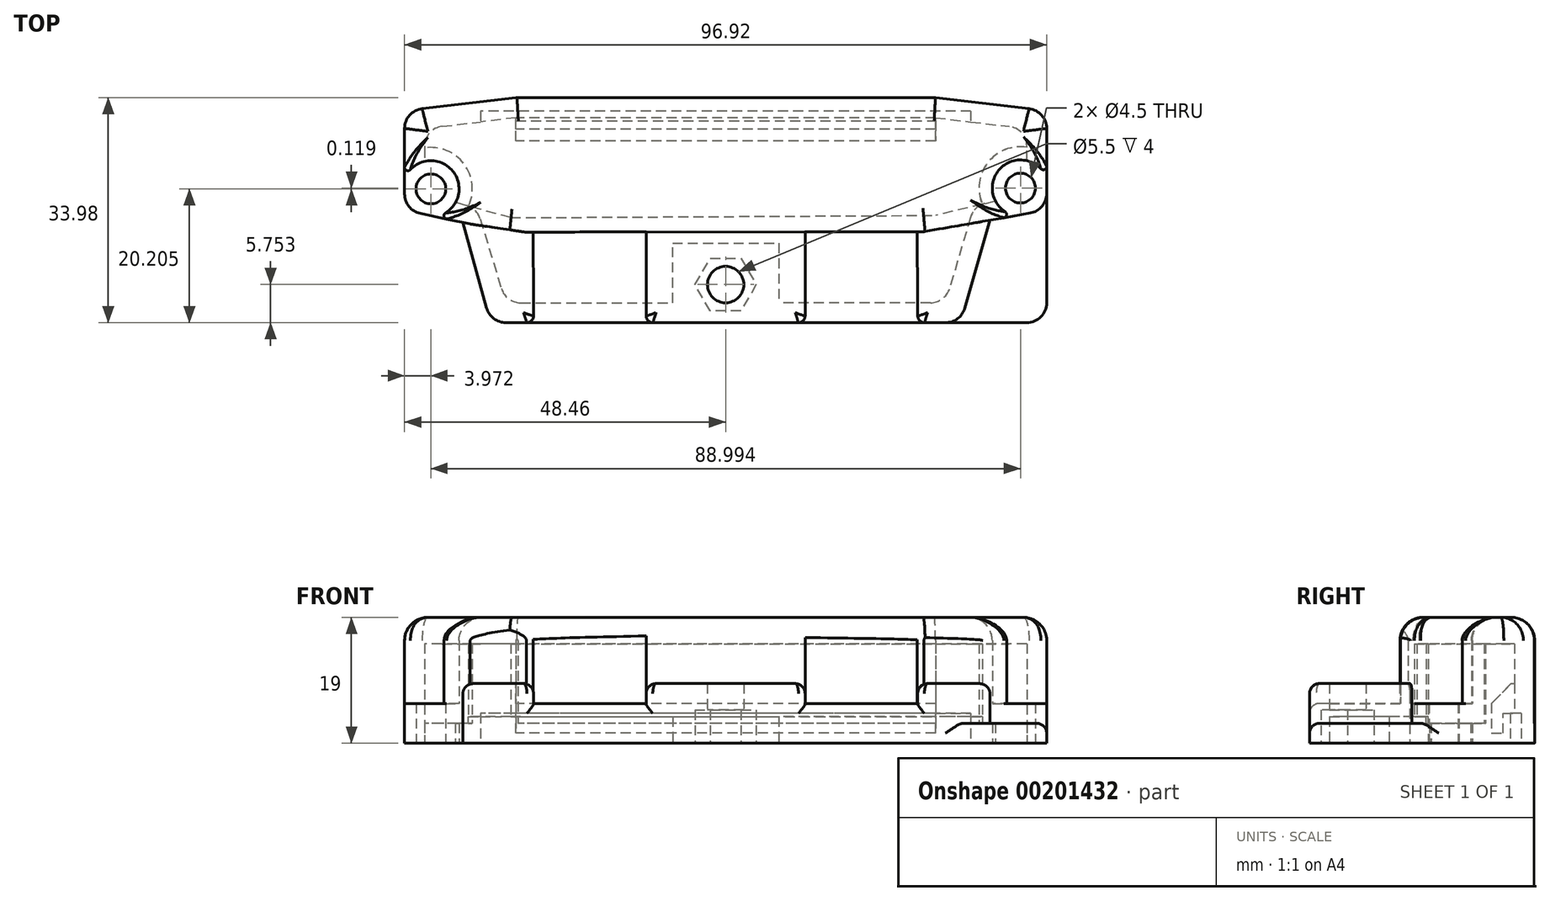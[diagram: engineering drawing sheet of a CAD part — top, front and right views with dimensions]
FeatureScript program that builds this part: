
annotation { "Feature Type Name" : "Feature", "Feature Type Description" : "" }
export const myFeature = defineFeature(function(context is Context, id is Id, definition is map)
    precondition{}
    {
        {
            var Q0;
            Q0=qCreatedBy(makeId("Top.planeOp"),FACE);
            var sketch = newSketch(context, id + "F0", { "sketchPlane" : qUnion([Q0])});
            skLineSegment(sketch, "E0.bottom", {"start": v(31.33, 16.99) * mm, "end": v(-31.32, 16.99) * mm});
            skLineSegment(sketch, "E0.left", {"start": v(48.46, 12.34) * mm, "end": v(48.46, 2.53) * mm});
            skLineSegment(sketch, "E0.right", {"start": v(-48.46, 12.34) * mm, "end": v(-48.46, 2.43) * mm});
            skPoint(sketch, "E0.middle", {"position": v(0, 0) * mm});
            skLineSegment(sketch, "E1", {"start": v(-45.8, 15.32) * mm, "end": v(-31.67, 16.97) * mm});
            skLineSegment(sketch, "E2", {"start": v(45.81, 15.32) * mm, "end": v(31.68, 16.97) * mm});
            skPoint(sketch, "E3.orphan", {"position": v(-48.46, 16.99) * mm});
            skPoint(sketch, "E4.orphan", {"position": v(48.46, 16.99) * mm});
            skPoint(sketch, "E5.visualSharp", {"position": v(-48.46, 15.01) * mm});
            skArc(sketch, "E5.filletArc", {"start": v(-45.8, 15.32) * mm, "mid": v(-47.7, 14.34) * mm, "end": v(-48.46, 12.34) * mm});
            skPoint(sketch, "E6.visualSharp", {"position": v(-48.46, -16.99) * mm});
            skPoint(sketch, "E7.visualSharp", {"position": v(48.46, -16.99) * mm});
            skPoint(sketch, "E8.visualSharp", {"position": v(48.46, 15.01) * mm});
            skArc(sketch, "E8.filletArc", {"start": v(48.46, 12.34) * mm, "mid": v(47.7, 14.34) * mm, "end": v(45.81, 15.32) * mm});
            skPoint(sketch, "E9.visualSharp", {"position": v(31.5, 16.99) * mm});
            skArc(sketch, "E9.filletArc", {"start": v(31.68, 16.97) * mm, "mid": v(31.5, 16.98) * mm, "end": v(31.33, 16.99) * mm});
            skPoint(sketch, "E10.visualSharp", {"position": v(-31.5, 16.99) * mm});
            skArc(sketch, "E10.filletArc", {"start": v(-31.32, 16.99) * mm, "mid": v(-31.5, 16.98) * mm, "end": v(-31.67, 16.97) * mm});
            skLineSegment(sketch, "E11", {"start": v(-39.66, -1.86) * mm, "end": v(-46.08, -0.5) * mm});
            skLineSegment(sketch, "E12", {"start": v(-39.66, -1.86) * mm, "end": v(-36.07, -14.79) * mm});
            skLineSegment(sketch, "E13", {"start": v(39.6, -1.52) * mm, "end": v(45.97, -0.43) * mm});
            skPoint(sketch, "E13.endSnap0", {"position": v(48.46, -0.82) * mm});
            skLineSegment(sketch, "E14", {"start": v(39.6, -1.52) * mm, "end": v(36.06, -14.76) * mm});
            skPoint(sketch, "E15.orphan", {"position": v(30.72, -3.04) * mm});
            skPoint(sketch, "E16.orphan", {"position": v(-30.85, -3.72) * mm});
            skLineSegment(sketch, "E17", {"start": v(-33.18, -16.99) * mm, "end": v(33.16, -16.99) * mm});
            skPoint(sketch, "E7.filletArc.end.orphan", {"position": v(48.46, -13.99) * mm});
            skPoint(sketch, "E18.visualSharp", {"position": v(-48.46, 0) * mm});
            skArc(sketch, "E18.filletArc", {"start": v(-48.46, 2.43) * mm, "mid": v(-47.8, 0.54) * mm, "end": v(-46.08, -0.5) * mm});
            skPoint(sketch, "E19.visualSharp", {"position": v(-35.46, -16.99) * mm});
            skArc(sketch, "E19.filletArc", {"start": v(-36.07, -14.79) * mm, "mid": v(-35, -16.37) * mm, "end": v(-33.18, -16.99) * mm});
            skPoint(sketch, "E20.visualSharp", {"position": v(35.46, -16.99) * mm});
            skArc(sketch, "E20.filletArc", {"start": v(33.16, -16.99) * mm, "mid": v(34.99, -16.37) * mm, "end": v(36.06, -14.76) * mm});
            skPoint(sketch, "E21.visualSharp", {"position": v(48.46, 0) * mm});
            skArc(sketch, "E21.filletArc", {"start": v(45.97, -0.43) * mm, "mid": v(47.76, 0.6) * mm, "end": v(48.46, 2.53) * mm});
            skCircle(sketch, "E22", {"center": v(44.5, 3.33) * mm, "radius": 2.25 * mm});
            skCircle(sketch, "E23", {"center": v(-44.49, 3.22) * mm, "radius": 2.25 * mm});
            skPoint(sketch, "E24.orphan", {"position": v(-47.8, 0.54) * mm});
            skPoint(sketch, "E25.orphan", {"position": v(47.76, 0.6) * mm});
            skLineSegment(sketch, "E26", {"start": v(-45.46, 12.34) * mm, "end": v(-31.32, 13.99) * mm});
            skLineSegment(sketch, "E27", {"start": v(-31.32, 13.99) * mm, "end": v(31.33, 13.99) * mm});
            skLineSegment(sketch, "E28", {"start": v(31.33, 13.99) * mm, "end": v(45.46, 12.34) * mm});
            skLineSegment(sketch, "E29", {"start": v(45.46, 7.47) * mm, "end": v(45.46, 12.34) * mm});
            skLineSegment(sketch, "E30", {"start": v(-45.46, 12.34) * mm, "end": v(-45.46, 7.35) * mm});
            skLineSegment(sketch, "E31", {"start": v(33.16, -13.99) * mm, "end": v(8, -13.99) * mm});
            skLineSegment(sketch, "E32", {"start": v(37.48, 0.6) * mm, "end": v(33.16, -13.99) * mm});
            skLineSegment(sketch, "E33", {"start": v(37.48, 0.6) * mm, "end": v(40.73, 1.39) * mm});
            skLineSegment(sketch, "E34", {"start": v(-37.53, 0.26) * mm, "end": v(-40.78, 1.15) * mm});
            skLineSegment(sketch, "E35", {"start": v(-37.53, 0.26) * mm, "end": v(-33.18, -13.99) * mm});
            skArc(sketch, "E36", {"start": v(-47.81, 0.57) * mm, "mid": v(-47.8, 0.56) * mm, "end": v(-47.8, 0.54) * mm});
            skArc(sketch, "E37.trimOffspring", {"start": v(-40.78, 1.15) * mm, "mid": v(-41.1, 5.78) * mm, "end": v(-45.46, 7.35) * mm});
            skArc(sketch, "E38", {"start": v(45.46, 7.47) * mm, "mid": v(41.15, 5.94) * mm, "end": v(40.73, 1.39) * mm});
            skLineSegment(sketch, "E39.trimOffspring", {"start": v(47.76, 0.6) * mm, "end": v(47.76, 0.6) * mm});
            skPoint(sketch, "E40.middle", {"position": v(1, -9.99) * mm});
            skPoint(sketch, "E41.start.orphan", {"position": v(0, -13.99) * mm});
            skLineSegment(sketch, "E42.0", {"start": v(-2.3, -7.24) * mm, "end": v(2.3, -7.24) * mm});
            skLineSegment(sketch, "E42.1", {"start": v(2.3, -7.24) * mm, "end": v(4.62, -11.24) * mm});
            skLineSegment(sketch, "E42.2", {"start": v(4.62, -11.24) * mm, "end": v(2.3, -15.24) * mm});
            skLineSegment(sketch, "E42.3", {"start": v(2.3, -15.24) * mm, "end": v(-2.3, -15.24) * mm});
            skLineSegment(sketch, "E42.4", {"start": v(-2.3, -15.24) * mm, "end": v(-4.62, -11.24) * mm});
            skLineSegment(sketch, "E42.5", {"start": v(-4.62, -11.24) * mm, "end": v(-2.3, -7.24) * mm});
            skPoint(sketch, "E42.0.midPoint", {"position": v(0, -7.24) * mm});
            skPoint(sketch, "E43.start.orphan", {"position": v(0, -8.49) * mm});
            skLineSegment(sketch, "E44", {"start": v(33.16, -16.99) * mm, "end": v(45.46, -16.99) * mm});
            skLineSegment(sketch, "E45", {"start": v(48.46, -13.99) * mm, "end": v(48.46, 2.53) * mm});
            skArc(sketch, "E46.filletArc", {"start": v(45.46, -16.99) * mm, "mid": v(47.58, -16.1) * mm, "end": v(48.46, -13.99) * mm});
            skPoint(sketch, "E47.start.orphan", {"position": v(0, 13.99) * mm});
            skLineSegment(sketch, "E48", {"start": v(0, 13.99) * mm, "end": v(0, 14.99) * mm});
            skLineSegment(sketch, "E49", {"start": v(0, 14.99) * mm, "end": v(37, 14.99) * mm});
            skLineSegment(sketch, "E50", {"start": v(0, 14.99) * mm, "end": v(-37, 14.99) * mm});
            skLineSegment(sketch, "E51", {"start": v(-37, 14.99) * mm, "end": v(-37, 13.33) * mm});
            skLineSegment(sketch, "E52", {"start": v(37, 14.99) * mm, "end": v(37, 13.33) * mm});
            skLineSegment(sketch, "E53", {"start": v(-8, -13.99) * mm, "end": v(-8, -4.99) * mm});
            skLineSegment(sketch, "E54", {"start": v(-8, -4.99) * mm, "end": v(8, -4.99) * mm});
            skLineSegment(sketch, "E55", {"start": v(-33.18, -13.99) * mm, "end": v(-8, -13.99) * mm});
            skLineSegment(sketch, "E56", {"start": v(8, -4.99) * mm, "end": v(8, -13.99) * mm});
            skSolve(sketch);
        }
        {
            var Q0;
            Q0 = qSketchRegion(id + "F0", true);
            extrude(context, id + "F1", {"entities" : qUnion([Q0]), "depth" : 3 * mm});
        }
        {
            var Q0;
            Q0=makeQuery(id+"F1.opExtrude","CAP_FACE",FACE,{"disambiguationData":[OSD([sQuery(id+"F0.wireOp",EDGE,"E0.bottom"),sQuery(id+"F0.wireOp",EDGE,"E0.left"),sQuery(id+"F0.wireOp",EDGE,"E0.right"),sQuery(id+"F0.wireOp",EDGE,"E1"),sQuery(id+"F0.wireOp",EDGE,"E2"),sQuery(id+"F0.wireOp",EDGE,"E5.filletArc"),sQuery(id+"F0.wireOp",EDGE,"E8.filletArc"),sQuery(id+"F0.wireOp",EDGE,"E9.filletArc"),sQuery(id+"F0.wireOp",EDGE,"E10.filletArc"),sQuery(id+"F0.wireOp",EDGE,"E11"),sQuery(id+"F0.wireOp",EDGE,"E12"),sQuery(id+"F0.wireOp",EDGE,"E17"),sQuery(id+"F0.wireOp",EDGE,"E18.filletArc"),sQuery(id+"F0.wireOp",EDGE,"E19.filletArc"),sQuery(id+"F0.wireOp",EDGE,"E22"),sQuery(id+"F0.wireOp",EDGE,"E23"),sQuery(id+"F0.wireOp",EDGE,"E26"),sQuery(id+"F0.wireOp",EDGE,"E27"),sQuery(id+"F0.wireOp",EDGE,"E28"),sQuery(id+"F0.wireOp",EDGE,"E29"),sQuery(id+"F0.wireOp",EDGE,"E30"),sQuery(id+"F0.wireOp",EDGE,"E31"),sQuery(id+"F0.wireOp",EDGE,"E32"),sQuery(id+"F0.wireOp",EDGE,"E33"),sQuery(id+"F0.wireOp",EDGE,"E34"),sQuery(id+"F0.wireOp",EDGE,"E35"),sQuery(id+"F0.wireOp",EDGE,"E37.trimOffspring"),sQuery(id+"F0.wireOp",EDGE,"E38"),sQuery(id+"F0.wireOp",EDGE,"E40.bottom"),sQuery(id+"F0.wireOp",EDGE,"E40.left"),sQuery(id+"F0.wireOp",EDGE,"E40.right"),sQuery(id+"F0.wireOp",EDGE,"2695b193-9afb-4e26-9978-a2569f4f271c.trimOffspring"),sQuery(id+"F0.wireOp",EDGE,"E42.0"),sQuery(id+"F0.wireOp",EDGE,"E42.1"),sQuery(id+"F0.wireOp",EDGE,"E42.2"),sQuery(id+"F0.wireOp",EDGE,"E42.3"),sQuery(id+"F0.wireOp",EDGE,"E42.4"),sQuery(id+"F0.wireOp",EDGE,"E42.5"),sQuery(id+"F0.wireOp",EDGE,"E44"),sQuery(id+"F0.wireOp",EDGE,"E45"),sQuery(id+"F0.wireOp",EDGE,"E46.filletArc")])],"isStart":false});
            var sketch = newSketch(context, id + "F2", { "sketchPlane" : qUnion([Q0])});
            skArc(sketch, "E57", {"start": v(45.46, 9.51) * mm, "mid": v(39.58, 7.18) * mm, "end": v(38.74, 0.91) * mm});
            skLineSegment(sketch, "E58", {"start": v(48.46, 8.17) * mm, "end": v(48.46, 0) * mm});
            skLineSegment(sketch, "E59", {"start": v(-44.15, 5.44) * mm, "end": v(-44.49, 3.22) * mm});
            skArc(sketch, "E60", {"start": v(-38.8, 0.6) * mm, "mid": v(-39.5, 6.99) * mm, "end": v(-45.46, 9.39) * mm});
            skArc(sketch, "E61", {"start": v(-48.46, 2.43) * mm, "mid": v(-47.8, 0.54) * mm, "end": v(-46.08, -0.5) * mm});
            skLineSegment(sketch, "E62", {"start": v(-46.08, -0.5) * mm, "end": v(-39.66, -1.86) * mm});
            skLineSegment(sketch, "E63", {"start": v(-39.66, -1.86) * mm, "end": v(-36.07, -14.79) * mm});
            skArc(sketch, "E64", {"start": v(-36.07, -14.79) * mm, "mid": v(-35, -16.37) * mm, "end": v(-33.18, -16.99) * mm});
            skLineSegment(sketch, "E65", {"start": v(-33.18, -16.99) * mm, "end": v(45.46, -16.99) * mm});
            skArc(sketch, "E66", {"start": v(45.46, -16.99) * mm, "mid": v(47.58, -16.1) * mm, "end": v(48.46, -13.99) * mm});
            skLineSegment(sketch, "E67", {"start": v(48.46, -13.99) * mm, "end": v(48.46, -1.5) * mm});
            skLineSegment(sketch, "E68", {"start": v(48.46, 8.17) * mm, "end": v(48.46, 12.34) * mm});
            skArc(sketch, "E69", {"start": v(48.46, 12.34) * mm, "mid": v(47.7, 14.34) * mm, "end": v(45.81, 15.32) * mm});
            skLineSegment(sketch, "E70", {"start": v(45.81, 15.32) * mm, "end": v(31.68, 16.97) * mm});
            skLineSegment(sketch, "E71", {"start": v(31.68, 16.97) * mm, "end": v(-31.32, 16.99) * mm});
            skLineSegment(sketch, "E72", {"start": v(-31.32, 16.99) * mm, "end": v(-31.67, 16.97) * mm});
            skLineSegment(sketch, "E73", {"start": v(-31.67, 16.97) * mm, "end": v(-45.8, 15.32) * mm});
            skArc(sketch, "E74", {"start": v(-45.8, 15.32) * mm, "mid": v(-47.7, 14.34) * mm, "end": v(-48.46, 12.34) * mm});
            skLineSegment(sketch, "E75", {"start": v(-48.46, 12.34) * mm, "end": v(-48.46, 2.43) * mm});
            skLineSegment(sketch, "E76", {"start": v(-38.8, 0.6) * mm, "end": v(-37.53, 0.26) * mm});
            skLineSegment(sketch, "E77", {"start": v(-37.53, 0.26) * mm, "end": v(-33.18, -13.99) * mm});
            skLineSegment(sketch, "E78", {"start": v(-6, -13.99) * mm, "end": v(-33.18, -13.99) * mm});
            skLineSegment(sketch, "E79", {"start": v(33.16, -13.99) * mm, "end": v(33.16, -13.99) * mm});
            skLineSegment(sketch, "E80", {"start": v(33.16, -13.99) * mm, "end": v(37.48, 0.6) * mm});
            skLineSegment(sketch, "E81", {"start": v(37.48, 0.6) * mm, "end": v(38.74, 0.91) * mm});
            skCircle(sketch, "E82", {"center": v(44.5, 3.33) * mm, "radius": 2.25 * mm});
            skCircle(sketch, "E83", {"center": v(-44.49, 3.22) * mm, "radius": 2.25 * mm});
            skArc(sketch, "E84", {"start": v(-47.81, 0.57) * mm, "mid": v(-47.8, 0.56) * mm, "end": v(-47.8, 0.54) * mm});
            skLineSegment(sketch, "E85", {"start": v(-45.46, 9.39) * mm, "end": v(-45.46, 12.34) * mm});
            skLineSegment(sketch, "E86", {"start": v(45.46, 12.34) * mm, "end": v(45.46, 12.34) * mm});
            skLineSegment(sketch, "E87", {"start": v(45.46, 12.34) * mm, "end": v(45.46, 9.51) * mm});
            skLineSegment(sketch, "E88", {"start": v(2.3, -7.24) * mm, "end": v(4.62, -11.24) * mm});
            skLineSegment(sketch, "E89", {"start": v(4.62, -11.24) * mm, "end": v(2.3, -15.24) * mm});
            skLineSegment(sketch, "E90", {"start": v(2.3, -15.24) * mm, "end": v(-2.3, -15.24) * mm});
            skLineSegment(sketch, "E91", {"start": v(-2.3, -15.24) * mm, "end": v(-4.62, -11.24) * mm});
            skLineSegment(sketch, "E92", {"start": v(-4.62, -11.24) * mm, "end": v(-2.3, -7.24) * mm});
            skLineSegment(sketch, "E93", {"start": v(-2.3, -7.24) * mm, "end": v(2.3, -7.24) * mm});
            skLineSegment(sketch, "E94", {"start": v(48.46, 4.89) * mm, "end": v(48.46, 1.78) * mm});
            skLineSegment(sketch, "E95", {"start": v(-48.46, 4.72) * mm, "end": v(-48.46, 2.43) * mm});
            skLineSegment(sketch, "E96", {"start": v(-46.08, -0.5) * mm, "end": v(-43.81, -0.98) * mm});
            skLineSegment(sketch, "E97", {"start": v(-48.46, 8.04) * mm, "end": v(-48.46, 4.72) * mm});
            skLineSegment(sketch, "E98", {"start": v(-48.46, 8.04) * mm, "end": v(-48.46, 2.43) * mm});
            skLineSegment(sketch, "E99", {"start": v(-45.46, 12.34) * mm, "end": v(-45.46, 9.39) * mm});
            skLineSegment(sketch, "E100", {"start": v(-37.53, 0.26) * mm, "end": v(-38.8, 0.6) * mm});
            skLineSegment(sketch, "E101", {"start": v(-45.46, 9.39) * mm, "end": v(-45.46, 7.35) * mm});
            skLineSegment(sketch, "E102", {"start": v(-38.8, 0.6) * mm, "end": v(-40.78, 1.15) * mm});
            skLineSegment(sketch, "E103", {"start": v(45.46, -16.99) * mm, "end": v(35.46, -16.99) * mm});
            skLineSegment(sketch, "E104", {"start": v(35.46, -16.99) * mm, "end": v(39.9, -1.51) * mm});
            skLineSegment(sketch, "E105", {"start": v(48.46, 0) * mm, "end": v(48.46, 0.5) * mm});
            skLineSegment(sketch, "E106", {"start": v(39.9, -1.51) * mm, "end": v(48.46, 0) * mm});
            skSolve(sketch);
        }
        {
            var Q0;
            {var subQ0=sQuery(id+"F2.wireOp",EDGE,"E57");Q0=makeQuery(id+"F2.imprint","IMPRINT",FACE,{"disambiguationData":[TD([[makeQuery(id+"F2.imprint","IMPRINT",EDGE,{"derivedFrom":subQ0}),1.0]])]});}
            var Q1;
            Q1=makeQuery(id+"F2.imprint","IMPRINT",FACE,{"disambiguationData":[TD([[makeQuery(id+"F2.imprint","IMPRINT",EDGE,{"derivedFrom":sQuery(id+"F2.wireOp",EDGE,"E60")}),1.0]])]});
            var Q2;
            Q2=makeQuery(id+"F2.imprint","IMPRINT",FACE,{"disambiguationData":[TD([[makeQuery(id+"F2.imprint","IMPRINT",EDGE,{"derivedFrom":sQuery(id+"F2.wireOp",EDGE,"E62")}),-1.0]])]});
            extrude(context, id + "F3", {"entities" : qUnion([Q0, Q1, Q2]), "operationType" : NewBodyOperationType.ADD, "depth" : 1.5 * mm});
        }
        {
            var Q0;
            Q0=makeQuery(id+"F3.opExtrude","CAP_FACE",FACE,{"disambiguationData":[OSD([sQuery(id+"F0.wireOp",EDGE,"E26"),sQuery(id+"F0.wireOp",EDGE,"E28"),sQuery(id+"F0.wireOp",EDGE,"E49"),sQuery(id+"F0.wireOp",EDGE,"E50"),sQuery(id+"F0.wireOp",EDGE,"E51"),sQuery(id+"F0.wireOp",EDGE,"E52"),sQuery(id+"F2.wireOp",EDGE,"E57"),sQuery(id+"F2.wireOp",EDGE,"E58"),sQuery(id+"F2.wireOp",EDGE,"E60"),sQuery(id+"F2.wireOp",EDGE,"E62"),sQuery(id+"F2.wireOp",EDGE,"E63"),sQuery(id+"F2.wireOp",EDGE,"E64"),sQuery(id+"F2.wireOp",EDGE,"E65"),sQuery(id+"F2.wireOp",EDGE,"E66"),sQuery(id+"F2.wireOp",EDGE,"E67"),sQuery(id+"F2.wireOp",EDGE,"E68"),sQuery(id+"F2.wireOp",EDGE,"E69"),sQuery(id+"F2.wireOp",EDGE,"E70"),sQuery(id+"F2.wireOp",EDGE,"E71"),sQuery(id+"F2.wireOp",EDGE,"E72"),sQuery(id+"F2.wireOp",EDGE,"E73"),sQuery(id+"F2.wireOp",EDGE,"E74"),sQuery(id+"F2.wireOp",EDGE,"E75"),sQuery(id+"F2.wireOp",EDGE,"E77"),sQuery(id+"F2.wireOp",EDGE,"E78"),sQuery(id+"F2.wireOp",EDGE,"VIfrpRYv-TWeq-2EBO-15lD-uvVJp7NSde8M"),sQuery(id+"F2.wireOp",EDGE,"AaESwfpV-ugF7-WlIc-K4uN-DpENZ3SdzwdN"),sQuery(id+"F2.wireOp",EDGE,"CHQ85Ftc-0NwL-8PEb-PDUD-3G7g8Jiz6bGZ"),sQuery(id+"F2.wireOp",EDGE,"E79"),sQuery(id+"F2.wireOp",EDGE,"E80"),sQuery(id+"F2.wireOp",EDGE,"E81"),sQuery(id+"F2.wireOp",EDGE,"E82"),sQuery(id+"F2.wireOp",EDGE,"E83"),sQuery(id+"F2.wireOp",EDGE,"E84"),sQuery(id+"F2.wireOp",EDGE,"E87"),sQuery(id+"F2.wireOp",EDGE,"E88"),sQuery(id+"F2.wireOp",EDGE,"E89"),sQuery(id+"F2.wireOp",EDGE,"E90"),sQuery(id+"F2.wireOp",EDGE,"E91"),sQuery(id+"F2.wireOp",EDGE,"E92"),sQuery(id+"F2.wireOp",EDGE,"E93"),sQuery(id+"F2.wireOp",EDGE,"E94"),sQuery(id+"F2.wireOp",EDGE,"E61"),sQuery(id+"F2.wireOp",EDGE,"E96"),sQuery(id+"F2.wireOp",EDGE,"E98"),sQuery(id+"F2.wireOp",EDGE,"E99"),sQuery(id+"F2.wireOp",EDGE,"E100")])],"isStart":false});
            var sketch = newSketch(context, id + "F4", { "sketchPlane" : qUnion([Q0])});
            skLineSegment(sketch, "E107", {"start": v(-31.67, 13.97) * mm, "end": v(-37, 13.33) * mm});
            skLineSegment(sketch, "E108", {"start": v(31.68, 13.97) * mm, "end": v(37, 13.33) * mm});
            skLineSegment(sketch, "E109", {"start": v(31.68, 13.97) * mm, "end": v(-31.67, 13.97) * mm});
            skSolve(sketch);
        }
        {
            var Q0;
            Q0 = qSketchRegion(id + "F4", true);
            var Q1;
            Q1=makeQuery(id+"F4.imprint","IMPRINT",FACE,{"disambiguationData":[TD([[makeQuery(id+"F4.imprint","IMPRINT",EDGE,{"derivedFrom":makeQuery(id+"F3.opExtrude","CAP_EDGE",EDGE,{"disambiguationData":[OSD([sQuery(id+"F2.wireOp",EDGE,"E57")])],"isStart":false})}),1.0]])]});
            var Q2;
            Q2=makeQuery(id+"F4.imprint","IMPRINT",FACE,{"disambiguationData":[TD([[makeQuery(id+"F4.imprint","IMPRINT",EDGE,{"derivedFrom":sQuery(id+"F4.wireOp",EDGE,"E107")}),-1.0]])]});
            extrude(context, id + "F5", {"entities" : qUnion([Q0, Q1, Q2]), "operationType" : NewBodyOperationType.ADD, "depth" : 1.5 * mm});
        }
        {
            var Q0;
            Q0=makeQuery(id+"F5.opExtrude","CAP_FACE",FACE,{"disambiguationData":[OSD([sQuery(id+"F0.wireOp",EDGE,"E26"),sQuery(id+"F0.wireOp",EDGE,"E28"),sQuery(id+"F2.wireOp",EDGE,"E57"),sQuery(id+"F2.wireOp",EDGE,"E58"),sQuery(id+"F2.wireOp",EDGE,"E60"),sQuery(id+"F2.wireOp",EDGE,"E62"),sQuery(id+"F2.wireOp",EDGE,"E63"),sQuery(id+"F2.wireOp",EDGE,"E64"),sQuery(id+"F2.wireOp",EDGE,"E65"),sQuery(id+"F2.wireOp",EDGE,"E66"),sQuery(id+"F2.wireOp",EDGE,"E67"),sQuery(id+"F2.wireOp",EDGE,"E68"),sQuery(id+"F2.wireOp",EDGE,"E69"),sQuery(id+"F2.wireOp",EDGE,"E70"),sQuery(id+"F2.wireOp",EDGE,"E71"),sQuery(id+"F2.wireOp",EDGE,"E72"),sQuery(id+"F2.wireOp",EDGE,"E73"),sQuery(id+"F2.wireOp",EDGE,"E74"),sQuery(id+"F2.wireOp",EDGE,"E75"),sQuery(id+"F2.wireOp",EDGE,"E77"),sQuery(id+"F2.wireOp",EDGE,"E78"),sQuery(id+"F2.wireOp",EDGE,"VIfrpRYv-TWeq-2EBO-15lD-uvVJp7NSde8M"),sQuery(id+"F2.wireOp",EDGE,"AaESwfpV-ugF7-WlIc-K4uN-DpENZ3SdzwdN"),sQuery(id+"F2.wireOp",EDGE,"CHQ85Ftc-0NwL-8PEb-PDUD-3G7g8Jiz6bGZ"),sQuery(id+"F2.wireOp",EDGE,"E79"),sQuery(id+"F2.wireOp",EDGE,"E80"),sQuery(id+"F2.wireOp",EDGE,"E81"),sQuery(id+"F2.wireOp",EDGE,"E82"),sQuery(id+"F2.wireOp",EDGE,"E83"),sQuery(id+"F2.wireOp",EDGE,"E84"),sQuery(id+"F2.wireOp",EDGE,"E87"),sQuery(id+"F2.wireOp",EDGE,"E88"),sQuery(id+"F2.wireOp",EDGE,"E89"),sQuery(id+"F2.wireOp",EDGE,"E90"),sQuery(id+"F2.wireOp",EDGE,"E91"),sQuery(id+"F2.wireOp",EDGE,"E92"),sQuery(id+"F2.wireOp",EDGE,"E93"),sQuery(id+"F2.wireOp",EDGE,"E94"),sQuery(id+"F2.wireOp",EDGE,"E61"),sQuery(id+"F2.wireOp",EDGE,"E96"),sQuery(id+"F2.wireOp",EDGE,"E98"),sQuery(id+"F2.wireOp",EDGE,"E99"),sQuery(id+"F2.wireOp",EDGE,"E100"),sQuery(id+"F4.wireOp",EDGE,"E107"),sQuery(id+"F4.wireOp",EDGE,"E108"),sQuery(id+"F4.wireOp",EDGE,"E109")])],"isStart":false});
            var sketch = newSketch(context, id + "F6", { "sketchPlane" : qUnion([Q0])});
            skLineSegment(sketch, "E110", {"start": v(38.74, 0.91) * mm, "end": v(31.68, -0.79) * mm});
            skLineSegment(sketch, "E111", {"start": v(-32.45, -1.14) * mm, "end": v(31.68, -0.79) * mm});
            skLineSegment(sketch, "E112", {"start": v(-32.45, -1.14) * mm, "end": v(-37.53, 0.26) * mm});
            skCircle(sketch, "E113", {"center": v(0, -11.24) * mm, "radius": 2.75 * mm});
            skLineSegment(sketch, "E114", {"start": v(0, -3.24) * mm, "end": v(12, -3.24) * mm});
            skLineSegment(sketch, "E115", {"start": v(-12, -3.24) * mm, "end": v(-12, -13.99) * mm});
            skLineSegment(sketch, "E116", {"start": v(-12, -13.99) * mm, "end": v(-12, -1.03) * mm});
            skLineSegment(sketch, "E117", {"start": v(12, -3.24) * mm, "end": v(12, -0.9) * mm});
            skLineSegment(sketch, "E118", {"start": v(12, -0.9) * mm, "end": v(12, -13.99) * mm});
            skLineSegment(sketch, "E119", {"start": v(29, -13.99) * mm, "end": v(28.93, -0.8) * mm});
            skLineSegment(sketch, "E120", {"start": v(-29, -13.99) * mm, "end": v(-29.07, -1.12) * mm});
            skLineSegment(sketch, "E121", {"start": v(12, -3.24) * mm, "end": v(28.94, -3.24) * mm});
            skLineSegment(sketch, "E122", {"start": v(-12, -3.24) * mm, "end": v(-29.07, -3.34) * mm});
            skLineSegment(sketch, "E123", {"start": v(29, -13.99) * mm, "end": v(29, -16.99) * mm});
            skLineSegment(sketch, "E124", {"start": v(12, -13.99) * mm, "end": v(12, -16.99) * mm});
            skLineSegment(sketch, "E125", {"start": v(-12, -13.99) * mm, "end": v(-12, -16.99) * mm});
            skLineSegment(sketch, "E126", {"start": v(-29, -13.99) * mm, "end": v(-29, -16.99) * mm});
            skLineSegment(sketch, "E127", {"start": v(0, -3.24) * mm, "end": v(-12, -3.24) * mm});
            skArc(sketch, "E128", {"start": v(48.46, 4.89) * mm, "mid": v(41.24, 6.05) * mm, "end": v(43.7, -0.84) * mm});
            skLineSegment(sketch, "E129", {"start": v(48.46, 4.89) * mm, "end": v(48.46, 1.78) * mm});
            skLineSegment(sketch, "E130", {"start": v(43.7, -0.84) * mm, "end": v(46.69, -0.31) * mm});
            skArc(sketch, "E131.trimOffspring", {"start": v(-43.81, -0.98) * mm, "mid": v(-41.2, 5.9) * mm, "end": v(-48.46, 4.72) * mm});
            skSolve(sketch);
        }
        {
            var Q0;
            {var subQ0=sQuery(id+"F2.wireOp",EDGE,"E106");var subQ1=sQuery(id+"F2.wireOp",EDGE,"E105");Q0=makeQuery(id+"F5.boolean.opBoolean","MERGE",EDGE,{"derivedFrom":[makeQuery(id+"F3.opExtrude","SWEPT_EDGE",EDGE,{"disambiguationData":[OSD([sQuery(id+"F0.wireOp",EDGE,"E0.left"),sQuery(id+"F0.wireOp",EDGE,"E45"),subQ1,subQ0])]}),makeQuery(id+"F5.opExtrude","SWEPT_EDGE",EDGE,{"disambiguationData":[OSD([sQuery(id+"F2.wireOp",EDGE,"E58"),sQuery(id+"F2.wireOp",EDGE,"E68"),sQuery(id+"F2.wireOp",EDGE,"E94"),subQ1,subQ0])]})]});}
            var Q1;
            {var subQ0=sQuery(id+"F2.wireOp",EDGE,"E104");var subQ1=sQuery(id+"F2.wireOp",EDGE,"E65");Q1=makeQuery(id+"F5.boolean.opBoolean","MERGE",EDGE,{"derivedFrom":[makeQuery(id+"F3.opExtrude","SWEPT_EDGE",EDGE,{"disambiguationData":[OSD([subQ1,sQuery(id+"F2.wireOp",EDGE,"E103"),subQ0])]}),makeQuery(id+"F5.opExtrude","SWEPT_EDGE",EDGE,{"disambiguationData":[OSD([subQ1,subQ0])]})]});}
            fillet(context, id + "F7", {"entities" : qUnion([Q0, Q1]), "radius" : 3 * mm, "tangentPropagation" : true, "allowEdgeOverflow" : false});
        }
        {
            var Q0;
            {var subQ0=sQuery(id+"F6.wireOp",EDGE,"E116");var subQ1=sQuery(id+"F6.wireOp",EDGE,"E111");var subQ2=makeQuery(id+"F6.imprint","INTERSECT",VERTEX,{"derivedFrom":[subQ1,subQ0]});Q0=makeQuery(id+"F6.imprint","IMPRINT",FACE,{"disambiguationData":[TD([[makeQuery(id+"F6.imprint","IMPRINT",EDGE,{"disambiguationData":[TD([[subQ2,1.0]])],"derivedFrom":subQ1}),-1.0]])]});}
            var Q1;
            {var subQ5=sQuery(id+"F6.wireOp",EDGE,"E121");Q1=makeQuery(id+"F6.imprint","IMPRINT",FACE,{"disambiguationData":[TD([[makeQuery(id+"F6.imprint","IMPRINT",EDGE,{"derivedFrom":subQ5}),1.0]])]});}
            var Q2;
            {var subQ6=makeQuery(id+"F5.opExtrude","CAP_EDGE",EDGE,{"disambiguationData":[OSD([sQuery(id+"F2.wireOp",EDGE,"VIfrpRYv-TWeq-2EBO-15lD-uvVJp7NSde8M")])],"isStart":false});Q2=makeQuery(id+"F6.imprint","IMPRINT",FACE,{"disambiguationData":[TD([[makeQuery(id+"F6.imprint","IMPRINT",EDGE,{"derivedFrom":subQ6}),-1.0]])]});}
            var Q3;
            {var subQ2=sQuery(id+"F6.wireOp",EDGE,"iywK1DUO-BXF0-jowS-0tvy-fWOFLAFzggMQ");Q3=makeQuery(id+"F6.imprint","IMPRINT",FACE,{"disambiguationData":[TD([[makeQuery(id+"F6.imprint","IMPRINT",EDGE,{"derivedFrom":subQ2}),1.0]])]});}
            var Q4;
            Q4=makeQuery(id+"F6.imprint","IMPRINT",FACE,{"disambiguationData":[TD([[makeQuery(id+"F6.imprint","IMPRINT",EDGE,{"derivedFrom":sQuery(id+"F6.wireOp",EDGE,"E113")}),-1.0]])]});
            var Q5;
            {var subQ4=sQuery(id+"F6.wireOp",EDGE,"E112");Q5=makeQuery(id+"F6.imprint","IMPRINT",FACE,{"disambiguationData":[TD([[makeQuery(id+"F6.imprint","IMPRINT",EDGE,{"derivedFrom":subQ4}),1.0]])]});}
            var Q6;
            {var subQ8=makeQuery(id+"F5.opExtrude","CAP_EDGE",EDGE,{"disambiguationData":[OSD([sQuery(id+"F2.wireOp",EDGE,"E80")])],"isStart":false});Q6=makeQuery(id+"F6.imprint","IMPRINT",FACE,{"disambiguationData":[TD([[makeQuery(id+"F6.imprint","IMPRINT",EDGE,{"derivedFrom":subQ8}),-1.0]])]});}
            var Q7;
            {var subQ3=sQuery(id+"F6.wireOp",EDGE,"E124");Q7=makeQuery(id+"F6.imprint","IMPRINT",FACE,{"disambiguationData":[TD([[makeQuery(id+"F6.imprint","IMPRINT",EDGE,{"derivedFrom":subQ3}),-1.0]])]});}
            var Q8;
            {var subQ1=sQuery(id+"F6.wireOp",EDGE,"E114");Q8=makeQuery(id+"F6.imprint","IMPRINT",FACE,{"disambiguationData":[TD([[makeQuery(id+"F6.imprint","IMPRINT",EDGE,{"derivedFrom":subQ1}),1.0]])]});}
            var Q9;
            {var subQ10=sQuery(id+"F6.wireOp",EDGE,"E123");Q9=makeQuery(id+"F6.imprint","IMPRINT",FACE,{"disambiguationData":[TD([[makeQuery(id+"F6.imprint","IMPRINT",EDGE,{"derivedFrom":subQ10}),1.0]])]});}
            var Q10;
            {var subQ7=sQuery(id+"F6.wireOp",EDGE,"E114");Q10=makeQuery(id+"F6.imprint","IMPRINT",FACE,{"disambiguationData":[TD([[makeQuery(id+"F6.imprint","IMPRINT",EDGE,{"derivedFrom":subQ7}),-1.0]])]});}
            extrude(context, id + "F8", {"entities" : qUnion([Q0, Q1, Q2, Q3, Q4, Q5, Q6, Q7, Q8, Q9, Q10]), "operationType" : NewBodyOperationType.ADD, "depth" : 3 * mm});
        }
        {
            var Q0;
            {var subQ4=sQuery(id+"F2.wireOp",EDGE,"E100");var subQ9=sQuery(id+"F6.wireOp",EDGE,"E122");var subQ10=sQuery(id+"F6.wireOp",EDGE,"BYT0MrnC-1C5n-uAkP-Muda-v8qsIDESU9eW");var subQ11=sQuery(id+"F6.wireOp",EDGE,"E119");var subQ12=sQuery(id+"F6.wireOp",EDGE,"iywK1DUO-BXF0-jowS-0tvy-fWOFLAFzggMQ");var subQ13=sQuery(id+"F6.wireOp",EDGE,"E120");var subQ14=sQuery(id+"F6.wireOp",EDGE,"E110");var subQ15=sQuery(id+"F6.wireOp",EDGE,"E111");var subQ16=sQuery(id+"F6.wireOp",EDGE,"E112");var subQ17=sQuery(id+"F6.wireOp",EDGE,"E118");var subQ18=sQuery(id+"F6.wireOp",EDGE,"E116");var subQ19=sQuery(id+"F6.wireOp",EDGE,"E121");Q0=makeQuery(id+"F8.boolean.opBoolean","SPLIT",FACE,{"disambiguationData":[TD([makeQuery(id+"F1.opExtrude","SWEPT_FACE",FACE,{"disambiguationData":[OSD([sQuery(id+"F0.wireOp",EDGE,"E31")])]})])],"derivedFrom":makeQuery(id+"F8.opExtrude","CAP_FACE",FACE,{"disambiguationData":[OSD([sQuery(id+"F0.wireOp",EDGE,"E26"),sQuery(id+"F0.wireOp",EDGE,"E28"),sQuery(id+"F2.wireOp",EDGE,"E57"),sQuery(id+"F2.wireOp",EDGE,"E58"),sQuery(id+"F2.wireOp",EDGE,"E60"),sQuery(id+"F2.wireOp",EDGE,"E62"),sQuery(id+"F2.wireOp",EDGE,"E63"),sQuery(id+"F2.wireOp",EDGE,"E64"),sQuery(id+"F2.wireOp",EDGE,"E65"),sQuery(id+"F2.wireOp",EDGE,"E68"),sQuery(id+"F2.wireOp",EDGE,"E69"),sQuery(id+"F2.wireOp",EDGE,"E70"),sQuery(id+"F2.wireOp",EDGE,"E71"),sQuery(id+"F2.wireOp",EDGE,"E72"),sQuery(id+"F2.wireOp",EDGE,"E73"),sQuery(id+"F2.wireOp",EDGE,"E74"),sQuery(id+"F2.wireOp",EDGE,"E75"),sQuery(id+"F2.wireOp",EDGE,"E82"),sQuery(id+"F2.wireOp",EDGE,"E83"),sQuery(id+"F2.wireOp",EDGE,"E84"),sQuery(id+"F2.wireOp",EDGE,"E87"),sQuery(id+"F2.wireOp",EDGE,"E94"),sQuery(id+"F2.wireOp",EDGE,"E61"),sQuery(id+"F2.wireOp",EDGE,"E96"),sQuery(id+"F2.wireOp",EDGE,"E98"),sQuery(id+"F2.wireOp",EDGE,"E99"),subQ4,sQuery(id+"F2.wireOp",EDGE,"E104"),sQuery(id+"F2.wireOp",EDGE,"E105"),sQuery(id+"F2.wireOp",EDGE,"E106"),sQuery(id+"F4.wireOp",EDGE,"E107"),sQuery(id+"F4.wireOp",EDGE,"E108"),sQuery(id+"F4.wireOp",EDGE,"E109"),subQ14,subQ15,subQ16,sQuery(id+"F6.wireOp",EDGE,"E113"),subQ18,subQ17,subQ12,subQ11,subQ10,subQ13,subQ19,subQ9])],"isStart":true})});}
            var sketch = newSketch(context, id + "F9", { "sketchPlane" : qUnion([Q0])});
            skLineSegment(sketch, "E132", {"start": v(12, 13.99) * mm, "end": v(29, 13.99) * mm});
            skLineSegment(sketch, "E133", {"start": v(-12, 13.99) * mm, "end": v(-29, 13.99) * mm});
            skLineSegment(sketch, "E134", {"start": v(-12, 13.99) * mm, "end": v(-8, 13.99) * mm});
            skLineSegment(sketch, "E135", {"start": v(-8, 13.99) * mm, "end": v(-8, 4.99) * mm});
            skLineSegment(sketch, "E136", {"start": v(-8, 4.99) * mm, "end": v(8, 4.99) * mm});
            skLineSegment(sketch, "E137", {"start": v(8, 4.99) * mm, "end": v(8, 13.99) * mm});
            skLineSegment(sketch, "E138", {"start": v(8, 13.99) * mm, "end": v(12, 13.99) * mm});
            skSolve(sketch);
        }
        {
            var Q0;
            Q0 = qSketchRegion(id + "F9", true);
            var Q1;
            {var subQ4=sQuery(id+"F6.wireOp",EDGE,"E111");Q1=makeQuery(id+"F9.imprint","IMPRINT",FACE,{"disambiguationData":[TD([[makeQuery(id+"F9.imprint","IMPRINT",EDGE,{"derivedFrom":makeQuery(id+"F8.opExtrude","CAP_EDGE",EDGE,{"disambiguationData":[OSD([subQ4])],"isStart":true})}),1.0]])]});}
            var Q2;
            Q2=makeQuery(id+"F9.imprint","IMPRINT",FACE,{"disambiguationData":[TD([[makeQuery(id+"F9.imprint","IMPRINT",EDGE,{"derivedFrom":sQuery(id+"F9.wireOp",EDGE,"E132")}),-1.0]])]});
            var Q3;
            Q3=makeQuery(id+"F9.imprint","IMPRINT",FACE,{"disambiguationData":[TD([[makeQuery(id+"F9.imprint","IMPRINT",EDGE,{"derivedFrom":sQuery(id+"F9.wireOp",EDGE,"E133")}),1.0]])]});
            extrude(context, id + "F10", {"entities" : qUnion([Q0, Q1, Q2, Q3]), "operationType" : NewBodyOperationType.ADD, "depth" : 2 * mm});
        }
        {
            var Q0;
            Q0=makeQuery(id+"F8.opExtrude","SWEPT_EDGE",EDGE,{"disambiguationData":[OSD([sQuery(id+"F2.wireOp",EDGE,"E58"),sQuery(id+"F2.wireOp",EDGE,"E68"),sQuery(id+"F2.wireOp",EDGE,"E94"),sQuery(id+"F2.wireOp",EDGE,"E105"),sQuery(id+"F2.wireOp",EDGE,"E106")])]});
            var Q1;
            Q1=makeQuery(id+"F8.opExtrude","SWEPT_EDGE",EDGE,{"disambiguationData":[OSD([sQuery(id+"F2.wireOp",EDGE,"E65"),sQuery(id+"F2.wireOp",EDGE,"E104")])]});
            fillet(context, id + "F11", {"entities" : qUnion([Q0, Q1]), "radius" : 3 * mm, "tangentPropagation" : true, "allowEdgeOverflow" : false});
        }
        {
            var Q0;
            Q0=makeQuery(id+"F8.opExtrude","SWEPT_EDGE",EDGE,{"disambiguationData":[OSD([sQuery(id+"F2.wireOp",EDGE,"E65"),sQuery(id+"F6.wireOp",EDGE,"E123")])]});
            var Q1;
            Q1=makeQuery(id+"F8.opExtrude","SWEPT_EDGE",EDGE,{"disambiguationData":[OSD([sQuery(id+"F2.wireOp",EDGE,"E65"),sQuery(id+"F6.wireOp",EDGE,"E124")])]});
            var Q2;
            Q2=makeQuery(id+"F8.opExtrude","SWEPT_EDGE",EDGE,{"disambiguationData":[OSD([sQuery(id+"F2.wireOp",EDGE,"E65"),sQuery(id+"F6.wireOp",EDGE,"E125")])]});
            var Q3;
            Q3=makeQuery(id+"F8.opExtrude","SWEPT_EDGE",EDGE,{"disambiguationData":[OSD([sQuery(id+"F2.wireOp",EDGE,"E65"),sQuery(id+"F6.wireOp",EDGE,"E126")])]});
            fillet(context, id + "F12", {"entities" : qUnion([Q0, Q1, Q2, Q3]), "radius" : 1 * mm, "tangentPropagation" : true, "allowEdgeOverflow" : false});
        }
        {
            var Q0;
            Q0=makeQuery(id+"F8.opExtrude","CAP_FACE",FACE,{"disambiguationData":[OSD([sQuery(id+"F0.wireOp",EDGE,"E26"),sQuery(id+"F0.wireOp",EDGE,"E28"),sQuery(id+"F2.wireOp",EDGE,"E57"),sQuery(id+"F2.wireOp",EDGE,"E58"),sQuery(id+"F2.wireOp",EDGE,"E60"),sQuery(id+"F2.wireOp",EDGE,"E62"),sQuery(id+"F2.wireOp",EDGE,"E63"),sQuery(id+"F2.wireOp",EDGE,"E64"),sQuery(id+"F2.wireOp",EDGE,"E65"),sQuery(id+"F2.wireOp",EDGE,"E68"),sQuery(id+"F2.wireOp",EDGE,"E69"),sQuery(id+"F2.wireOp",EDGE,"E70"),sQuery(id+"F2.wireOp",EDGE,"E71"),sQuery(id+"F2.wireOp",EDGE,"E72"),sQuery(id+"F2.wireOp",EDGE,"E73"),sQuery(id+"F2.wireOp",EDGE,"E74"),sQuery(id+"F2.wireOp",EDGE,"E75"),sQuery(id+"F2.wireOp",EDGE,"E87"),sQuery(id+"F2.wireOp",EDGE,"E94"),sQuery(id+"F2.wireOp",EDGE,"E96"),sQuery(id+"F2.wireOp",EDGE,"E98"),sQuery(id+"F2.wireOp",EDGE,"E99"),sQuery(id+"F2.wireOp",EDGE,"E100"),sQuery(id+"F2.wireOp",EDGE,"E104"),sQuery(id+"F2.wireOp",EDGE,"E105"),sQuery(id+"F2.wireOp",EDGE,"E106"),sQuery(id+"F4.wireOp",EDGE,"E107"),sQuery(id+"F4.wireOp",EDGE,"E108"),sQuery(id+"F4.wireOp",EDGE,"E109"),sQuery(id+"F6.wireOp",EDGE,"E110"),sQuery(id+"F6.wireOp",EDGE,"E111"),sQuery(id+"F6.wireOp",EDGE,"E112"),sQuery(id+"F6.wireOp",EDGE,"E113"),sQuery(id+"F6.wireOp",EDGE,"E116"),sQuery(id+"F6.wireOp",EDGE,"E118"),sQuery(id+"F6.wireOp",EDGE,"E119"),sQuery(id+"F6.wireOp",EDGE,"E120"),sQuery(id+"F6.wireOp",EDGE,"E121"),sQuery(id+"F6.wireOp",EDGE,"E122"),sQuery(id+"F6.wireOp",EDGE,"E123"),sQuery(id+"F6.wireOp",EDGE,"E124"),sQuery(id+"F6.wireOp",EDGE,"E125"),sQuery(id+"F6.wireOp",EDGE,"E126"),sQuery(id+"F6.wireOp",EDGE,"E128"),sQuery(id+"F6.wireOp",EDGE,"E131.trimOffspring")])],"isStart":false});
            var sketch = newSketch(context, id + "F13", { "sketchPlane" : qUnion([Q0])});
            skLineSegment(sketch, "E139", {"start": v(29.94, -3.24) * mm, "end": v(38.8, -1.7) * mm});
            skLineSegment(sketch, "E140", {"start": v(-38.55, -2.1) * mm, "end": v(-30.06, -3.34) * mm});
            skLineSegment(sketch, "E141", {"start": v(-30.06, -3.34) * mm, "end": v(29.94, -3.24) * mm});
            skLineSegment(sketch, "E142", {"start": v(38.8, -1.7) * mm, "end": v(39.9, -1.51) * mm});
            skLineSegment(sketch, "E143", {"start": v(-38.55, -2.1) * mm, "end": v(-39.66, -1.86) * mm});
            skSolve(sketch);
        }
        {
            var Q0;
            Q0=makeQuery(id+"F13.imprint","IMPRINT",FACE,{"disambiguationData":[TD([[makeQuery(id+"F13.imprint","IMPRINT",EDGE,{"derivedFrom":sQuery(id+"F13.wireOp",EDGE,"E139")}),1.0]])]});
            extrude(context, id + "F14", {"entities" : qUnion([Q0]), "operationType" : NewBodyOperationType.ADD, "depth" : 6 * mm});
        }
        {
            var Q0;
            Q0=makeQuery(id+"F14.opExtrude","CAP_FACE",FACE,{"disambiguationData":[OSD([sQuery(id+"F0.wireOp",EDGE,"E26"),sQuery(id+"F0.wireOp",EDGE,"E28"),sQuery(id+"F2.wireOp",EDGE,"E57"),sQuery(id+"F2.wireOp",EDGE,"E58"),sQuery(id+"F2.wireOp",EDGE,"E60"),sQuery(id+"F2.wireOp",EDGE,"E62"),sQuery(id+"F2.wireOp",EDGE,"E63"),sQuery(id+"F2.wireOp",EDGE,"E64"),sQuery(id+"F2.wireOp",EDGE,"E65"),sQuery(id+"F2.wireOp",EDGE,"E68"),sQuery(id+"F2.wireOp",EDGE,"E69"),sQuery(id+"F2.wireOp",EDGE,"E70"),sQuery(id+"F2.wireOp",EDGE,"E71"),sQuery(id+"F2.wireOp",EDGE,"E72"),sQuery(id+"F2.wireOp",EDGE,"E73"),sQuery(id+"F2.wireOp",EDGE,"E74"),sQuery(id+"F2.wireOp",EDGE,"E75"),sQuery(id+"F2.wireOp",EDGE,"E87"),sQuery(id+"F2.wireOp",EDGE,"E94"),sQuery(id+"F2.wireOp",EDGE,"E96"),sQuery(id+"F2.wireOp",EDGE,"E98"),sQuery(id+"F2.wireOp",EDGE,"E99"),sQuery(id+"F2.wireOp",EDGE,"E100"),sQuery(id+"F2.wireOp",EDGE,"E104"),sQuery(id+"F2.wireOp",EDGE,"E105"),sQuery(id+"F2.wireOp",EDGE,"E106"),sQuery(id+"F4.wireOp",EDGE,"E107"),sQuery(id+"F4.wireOp",EDGE,"E108"),sQuery(id+"F4.wireOp",EDGE,"E109"),sQuery(id+"F6.wireOp",EDGE,"E110"),sQuery(id+"F6.wireOp",EDGE,"E111"),sQuery(id+"F6.wireOp",EDGE,"E112"),sQuery(id+"F6.wireOp",EDGE,"E113"),sQuery(id+"F6.wireOp",EDGE,"E116"),sQuery(id+"F6.wireOp",EDGE,"E118"),sQuery(id+"F6.wireOp",EDGE,"E119"),sQuery(id+"F6.wireOp",EDGE,"E120"),sQuery(id+"F6.wireOp",EDGE,"E121"),sQuery(id+"F6.wireOp",EDGE,"E122"),sQuery(id+"F6.wireOp",EDGE,"E123"),sQuery(id+"F6.wireOp",EDGE,"E124"),sQuery(id+"F6.wireOp",EDGE,"E125"),sQuery(id+"F6.wireOp",EDGE,"E126"),sQuery(id+"F6.wireOp",EDGE,"E128"),sQuery(id+"F6.wireOp",EDGE,"E131.trimOffspring"),sQuery(id+"F13.wireOp",EDGE,"E139"),sQuery(id+"F13.wireOp",EDGE,"E140"),sQuery(id+"F13.wireOp",EDGE,"E141")])],"isStart":false});
            var sketch = newSketch(context, id + "F15", { "sketchPlane" : qUnion([Q0])});
            skSolve(sketch);
        }
        {
            var Q0;
            Q0=makeQuery(id+"F15.imprint","IMPRINT",FACE,{"disambiguationData":[TD([[makeQuery(id+"F15.imprint","IMPRINT",EDGE,{"derivedFrom":makeQuery(id+"F14.opExtrude","CAP_EDGE",EDGE,{"disambiguationData":[OSD([sQuery(id+"F6.wireOp",EDGE,"E110")])],"isStart":false})}),-1.0]])]});
            var Q1;
            Q1=makeQuery(id+"F15.imprint","IMPRINT",FACE,{"disambiguationData":[TD([[makeQuery(id+"F15.imprint","IMPRINT",EDGE,{"derivedFrom":makeQuery(id+"F14.opExtrude","CAP_EDGE",EDGE,{"disambiguationData":[OSD([sQuery(id+"F13.wireOp",EDGE,"E139")])],"isStart":false})}),1.0]])]});
            extrude(context, id + "F16", {"entities" : qUnion([Q0, Q1]), "operationType" : NewBodyOperationType.ADD, "depth" : 4 * mm});
        }
        {
            var Q0;
            {var subQ0=sQuery(id+"F4.wireOp",EDGE,"E109");Q0=makeQuery(id+"F14.boolean.opBoolean","MERGE",FACE,{"derivedFrom":[makeQuery(id+"F8.boolean.opBoolean","MERGE",FACE,{"derivedFrom":[makeQuery(id+"F5.opExtrude","SWEPT_FACE",FACE,{"disambiguationData":[OSD([subQ0])]}),makeQuery(id+"F8.opExtrude","SWEPT_FACE",FACE,{"disambiguationData":[OSD([subQ0])]})]}),makeQuery(id+"F14.opExtrude","SWEPT_FACE",FACE,{"disambiguationData":[OSD([subQ0])]})]});}
            var sketch = newSketch(context, id + "F17", { "sketchPlane" : qUnion([Q0])});
            skLineSegment(sketch, "E144", {"start": v(-31.67, 4.5) * mm, "end": v(-31.67, 7.5) * mm});
            skLineSegment(sketch, "E145", {"start": v(31.68, 7.5) * mm, "end": v(31.68, 4.5) * mm});
            skLineSegment(sketch, "E146", {"start": v(31.68, 7.5) * mm, "end": v(-31.67, 7.5) * mm});
            skLineSegment(sketch, "E147", {"start": v(31.68, 7.5) * mm, "end": v(31.68, 9) * mm});
            skLineSegment(sketch, "E148", {"start": v(31.68, 9) * mm, "end": v(-31.67, 9) * mm});
            skLineSegment(sketch, "E149", {"start": v(-31.67, 9) * mm, "end": v(-31.67, 7.5) * mm});
            skSolve(sketch);
        }
        {
            var Q0;
            Q0=makeQuery(id+"F17.imprint","IMPRINT",FACE,{"disambiguationData":[TD([[makeQuery(id+"F17.imprint","IMPRINT",EDGE,{"derivedFrom":sQuery(id+"F17.wireOp",EDGE,"E144")}),1.0]])]});
            var Q1;
            Q1=makeQuery(id+"F17.imprint","IMPRINT",FACE,{"disambiguationData":[TD([[makeQuery(id+"F17.imprint","IMPRINT",EDGE,{"derivedFrom":sQuery(id+"F17.wireOp",EDGE,"E146")}),-1.0]])]});
            extrude(context, id + "F18", {"entities" : qUnion([Q0, Q1]), "operationType" : NewBodyOperationType.ADD, "depth" : 3.5 * mm});
        }
        {
            var Q0;
            Q0=makeQuery(id+"F18.opExtrude","CAP_EDGE",EDGE,{"disambiguationData":[OSD([sQuery(id+"F17.wireOp",EDGE,"E148")])],"isStart":false});
            chamfer(context, id + "F19", {"entities" : qUnion([Q0]), "width" : 3 * mm, "tangentPropagation" : true});
        }
        {
            var Q0;
            {var subQ0=sQuery(id+"F4.wireOp",EDGE,"E109");Q0=makeQuery(id+"F18.boolean.opBoolean","MERGE",FACE,{"derivedFrom":[makeQuery(id+"F5.opExtrude","CAP_FACE",FACE,{"disambiguationData":[OSD([sQuery(id+"F0.wireOp",EDGE,"E26"),sQuery(id+"F0.wireOp",EDGE,"E28"),sQuery(id+"F2.wireOp",EDGE,"E57"),sQuery(id+"F2.wireOp",EDGE,"E58"),sQuery(id+"F2.wireOp",EDGE,"E60"),sQuery(id+"F2.wireOp",EDGE,"E62"),sQuery(id+"F2.wireOp",EDGE,"E63"),sQuery(id+"F2.wireOp",EDGE,"E64"),sQuery(id+"F2.wireOp",EDGE,"E65"),sQuery(id+"F2.wireOp",EDGE,"E68"),sQuery(id+"F2.wireOp",EDGE,"E69"),sQuery(id+"F2.wireOp",EDGE,"E70"),sQuery(id+"F2.wireOp",EDGE,"E71"),sQuery(id+"F2.wireOp",EDGE,"E72"),sQuery(id+"F2.wireOp",EDGE,"E73"),sQuery(id+"F2.wireOp",EDGE,"E74"),sQuery(id+"F2.wireOp",EDGE,"E75"),sQuery(id+"F2.wireOp",EDGE,"E77"),sQuery(id+"F2.wireOp",EDGE,"E78"),sQuery(id+"F2.wireOp",EDGE,"VIfrpRYv-TWeq-2EBO-15lD-uvVJp7NSde8M"),sQuery(id+"F2.wireOp",EDGE,"AaESwfpV-ugF7-WlIc-K4uN-DpENZ3SdzwdN"),sQuery(id+"F2.wireOp",EDGE,"CHQ85Ftc-0NwL-8PEb-PDUD-3G7g8Jiz6bGZ"),sQuery(id+"F2.wireOp",EDGE,"E79"),sQuery(id+"F2.wireOp",EDGE,"E80"),sQuery(id+"F2.wireOp",EDGE,"E81"),sQuery(id+"F2.wireOp",EDGE,"E82"),sQuery(id+"F2.wireOp",EDGE,"E83"),sQuery(id+"F2.wireOp",EDGE,"E84"),sQuery(id+"F2.wireOp",EDGE,"E87"),sQuery(id+"F2.wireOp",EDGE,"E88"),sQuery(id+"F2.wireOp",EDGE,"E89"),sQuery(id+"F2.wireOp",EDGE,"E90"),sQuery(id+"F2.wireOp",EDGE,"E91"),sQuery(id+"F2.wireOp",EDGE,"E92"),sQuery(id+"F2.wireOp",EDGE,"E93"),sQuery(id+"F2.wireOp",EDGE,"E94"),sQuery(id+"F2.wireOp",EDGE,"E61"),sQuery(id+"F2.wireOp",EDGE,"E96"),sQuery(id+"F2.wireOp",EDGE,"E98"),sQuery(id+"F2.wireOp",EDGE,"E99"),sQuery(id+"F2.wireOp",EDGE,"E100"),sQuery(id+"F2.wireOp",EDGE,"E104"),sQuery(id+"F2.wireOp",EDGE,"E105"),sQuery(id+"F2.wireOp",EDGE,"E106"),sQuery(id+"F4.wireOp",EDGE,"E107"),sQuery(id+"F4.wireOp",EDGE,"E108"),subQ0])],"isStart":true}),makeQuery(id+"F18.opExtrude","SWEPT_FACE",FACE,{"disambiguationData":[OSD([subQ0])]})]});}
            var sketch = newSketch(context, id + "F20", { "sketchPlane" : qUnion([Q0])});
            skLineSegment(sketch, "E150", {"start": v(31.68, -10.47) * mm, "end": v(31.68, -12.22) * mm});
            skLineSegment(sketch, "E151", {"start": v(31.68, -12.22) * mm, "end": v(-31.67, -12.22) * mm});
            skSolve(sketch);
        }
        {
            var Q0;
            Q0=makeQuery(id+"F20.imprint","IMPRINT",FACE,{"disambiguationData":[TD([[makeQuery(id+"F20.imprint","IMPRINT",EDGE,{"derivedFrom":sQuery(id+"F20.wireOp",EDGE,"E150")}),-1.0]])]});
            extrude(context, id + "F21", {"entities" : qUnion([Q0]), "operationType" : NewBodyOperationType.ADD, "depth" : 3 * mm});
        }
        {
            var Q0;
            {var subQ0=sQuery(id+"F2.wireOp",EDGE,"E78");var subQ1=sQuery(id+"F2.wireOp",EDGE,"E77");Q0=makeQuery(id+"F5.boolean.opBoolean","MERGE",EDGE,{"derivedFrom":[makeQuery(id+"F3.boolean.opBoolean","MERGE",EDGE,{"derivedFrom":[makeQuery(id+"F1.opExtrude","SWEPT_EDGE",EDGE,{"disambiguationData":[OSD([sQuery(id+"F0.wireOp",EDGE,"E35"),sQuery(id+"F0.wireOp",EDGE,"E55")])]}),makeQuery(id+"F3.opExtrude","SWEPT_EDGE",EDGE,{"disambiguationData":[OSD([subQ1,subQ0])]})]}),makeQuery(id+"F5.opExtrude","SWEPT_EDGE",EDGE,{"disambiguationData":[OSD([subQ1,subQ0])]})]});}
            var Q1;
            {var subQ0=sQuery(id+"F2.wireOp",EDGE,"E100");var subQ1=sQuery(id+"F2.wireOp",EDGE,"E77");Q1=makeQuery(id+"F5.boolean.opBoolean","MERGE",EDGE,{"derivedFrom":[makeQuery(id+"F3.boolean.opBoolean","MERGE",EDGE,{"derivedFrom":[makeQuery(id+"F1.opExtrude","SWEPT_EDGE",EDGE,{"disambiguationData":[OSD([sQuery(id+"F0.wireOp",EDGE,"E34"),sQuery(id+"F0.wireOp",EDGE,"E35")])]}),makeQuery(id+"F3.opExtrude","SWEPT_EDGE",EDGE,{"disambiguationData":[OSD([subQ1,subQ0])]})]}),makeQuery(id+"F5.opExtrude","SWEPT_EDGE",EDGE,{"disambiguationData":[OSD([subQ1,subQ0])]})]});}
            var Q2;
            {var subQ0=sQuery(id+"F2.wireOp",EDGE,"E99");var subQ1=sQuery(id+"F0.wireOp",EDGE,"E26");Q2=makeQuery(id+"F14.boolean.opBoolean","MERGE",EDGE,{"derivedFrom":[makeQuery(id+"F8.boolean.opBoolean","MERGE",EDGE,{"derivedFrom":[makeQuery(id+"F5.boolean.opBoolean","MERGE",EDGE,{"derivedFrom":[makeQuery(id+"F3.boolean.opBoolean","MERGE",EDGE,{"derivedFrom":[makeQuery(id+"F1.opExtrude","SWEPT_EDGE",EDGE,{"disambiguationData":[OSD([subQ1,sQuery(id+"F0.wireOp",EDGE,"E30")])]}),makeQuery(id+"F3.opExtrude","SWEPT_EDGE",EDGE,{"disambiguationData":[OSD([subQ1,subQ0])]})]}),makeQuery(id+"F5.opExtrude","SWEPT_EDGE",EDGE,{"disambiguationData":[OSD([subQ1,subQ0])]})]}),makeQuery(id+"F8.opExtrude","SWEPT_EDGE",EDGE,{"disambiguationData":[OSD([subQ1,subQ0])]})]}),makeQuery(id+"F14.opExtrude","SWEPT_EDGE",EDGE,{"disambiguationData":[OSD([subQ1,subQ0])]})]});}
            var Q3;
            {var subQ0=sQuery(id+"F2.wireOp",EDGE,"E80");var subQ1=sQuery(id+"F0.wireOp",EDGE,"E31");Q3=makeQuery(id+"F5.boolean.opBoolean","MERGE",EDGE,{"derivedFrom":[makeQuery(id+"F3.boolean.opBoolean","MERGE",EDGE,{"derivedFrom":[makeQuery(id+"F1.opExtrude","SWEPT_EDGE",EDGE,{"disambiguationData":[OSD([subQ1,sQuery(id+"F0.wireOp",EDGE,"E32")])]}),makeQuery(id+"F3.opExtrude","SWEPT_EDGE",EDGE,{"disambiguationData":[OSD([subQ1,subQ0])]})]}),makeQuery(id+"F5.opExtrude","SWEPT_EDGE",EDGE,{"disambiguationData":[OSD([subQ1,subQ0])]})]});}
            var Q4;
            {var subQ0=sQuery(id+"F2.wireOp",EDGE,"E81");var subQ1=sQuery(id+"F2.wireOp",EDGE,"E80");Q4=makeQuery(id+"F5.boolean.opBoolean","MERGE",EDGE,{"derivedFrom":[makeQuery(id+"F3.boolean.opBoolean","MERGE",EDGE,{"derivedFrom":[makeQuery(id+"F1.opExtrude","SWEPT_EDGE",EDGE,{"disambiguationData":[OSD([sQuery(id+"F0.wireOp",EDGE,"E32"),sQuery(id+"F0.wireOp",EDGE,"E33")])]}),makeQuery(id+"F3.opExtrude","SWEPT_EDGE",EDGE,{"disambiguationData":[OSD([subQ1,subQ0])]})]}),makeQuery(id+"F5.opExtrude","SWEPT_EDGE",EDGE,{"disambiguationData":[OSD([subQ1,subQ0])]})]});}
            var Q5;
            {var subQ0=sQuery(id+"F2.wireOp",EDGE,"E87");var subQ1=sQuery(id+"F0.wireOp",EDGE,"E28");Q5=makeQuery(id+"F14.boolean.opBoolean","MERGE",EDGE,{"derivedFrom":[makeQuery(id+"F8.boolean.opBoolean","MERGE",EDGE,{"derivedFrom":[makeQuery(id+"F5.boolean.opBoolean","MERGE",EDGE,{"derivedFrom":[makeQuery(id+"F3.boolean.opBoolean","MERGE",EDGE,{"derivedFrom":[makeQuery(id+"F1.opExtrude","SWEPT_EDGE",EDGE,{"disambiguationData":[OSD([subQ1,sQuery(id+"F0.wireOp",EDGE,"E29")])]}),makeQuery(id+"F3.opExtrude","SWEPT_EDGE",EDGE,{"disambiguationData":[OSD([subQ1,subQ0])]})]}),makeQuery(id+"F5.opExtrude","SWEPT_EDGE",EDGE,{"disambiguationData":[OSD([subQ1,subQ0])]})]}),makeQuery(id+"F8.opExtrude","SWEPT_EDGE",EDGE,{"disambiguationData":[OSD([subQ1,subQ0])]})]}),makeQuery(id+"F14.opExtrude","SWEPT_EDGE",EDGE,{"disambiguationData":[OSD([subQ1,subQ0])]})]});}
            fillet(context, id + "F22", {"entities" : qUnion([Q0, Q1, Q2, Q3, Q4, Q5]), "radius" : 3 * mm, "tangentPropagation" : true, "allowEdgeOverflow" : false});
        }
        {
            var Q0;
            Q0=makeQuery(id+"F8.opExtrude","CAP_EDGE",EDGE,{"disambiguationData":[OSD([sQuery(id+"F6.wireOp",EDGE,"E120")])],"isStart":false});
            var Q1;
            Q1=makeQuery(id+"F8.opExtrude","CAP_EDGE",EDGE,{"disambiguationData":[OSD([sQuery(id+"F2.wireOp",EDGE,"E64")])],"isStart":false});
            var Q2;
            {var subQ0=sQuery(id+"F2.wireOp",EDGE,"E65");var subQ1=makeQuery(id+"F5.opExtrude","CAP_EDGE",EDGE,{"disambiguationData":[OSD([subQ0])],"isStart":false});Q2=makeQuery(id+"F8.opExtrude","CAP_EDGE",EDGE,{"disambiguationData":[OSD([subQ0]),TDD([makeQuery(id+"F6.imprint","IMPRINT",EDGE,{"disambiguationData":[TD([[makeQuery(id+"F6.imprint","INTERSECT",VERTEX,{"derivedFrom":[subQ1,sQuery(id+"F6.wireOp",EDGE,"E124")]}),1.0]])],"derivedFrom":subQ1})])],"isStart":false});}
            var Q3;
            Q3=makeQuery(id+"F8.opExtrude","CAP_EDGE",EDGE,{"disambiguationData":[OSD([sQuery(id+"F2.wireOp",EDGE,"E104")])],"isStart":false});
            var Q4;
            {var subQ0=sQuery(id+"F2.wireOp",EDGE,"E65");var subQ3=sQuery(id+"F6.wireOp",EDGE,"E126");var subQ5=makeQuery(id+"F5.opExtrude","CAP_EDGE",EDGE,{"disambiguationData":[OSD([subQ0])],"isStart":false});Q4=makeQuery(id+"F8.boolean.opBoolean","SPLIT",EDGE,{"disambiguationData":[TD([makeQuery(id+"F8.opExtrude","SWEPT_FACE",FACE,{"disambiguationData":[OSD([subQ3])]})])],"derivedFrom":subQ5});}
            var Q5;
            {var subQ0=sQuery(id+"F2.wireOp",EDGE,"E65");var subQ4=sQuery(id+"F6.wireOp",EDGE,"E123");var subQ5=makeQuery(id+"F5.opExtrude","CAP_EDGE",EDGE,{"disambiguationData":[OSD([subQ0])],"isStart":false});Q5=makeQuery(id+"F8.boolean.opBoolean","SPLIT",EDGE,{"disambiguationData":[TD([makeQuery(id+"F8.opExtrude","SWEPT_FACE",FACE,{"disambiguationData":[OSD([subQ4])]})])],"derivedFrom":subQ5});}
            var Q6;
            Q6=makeQuery(id+"F1.opExtrude","CAP_EDGE",EDGE,{"disambiguationData":[OSD([sQuery(id+"F0.wireOp",EDGE,"E17"),sQuery(id+"F0.wireOp",EDGE,"E44")])],"isStart":false});
            fillet(context, id + "F23", {"entities" : qUnion([Q0, Q1, Q2, Q3, Q4, Q5, Q6]), "radius" : 1.5 * mm, "tangentPropagation" : true, "allowEdgeOverflow" : false});
        }
        {
            var Q0;
            {var subQ6=sQuery(id+"F6.wireOp",EDGE,"E113");Q0=makeQuery(id+"F8.boolean.opBoolean","SPLIT",FACE,{"disambiguationData":[TD([makeQuery(id+"F1.opExtrude","SWEPT_FACE",FACE,{"disambiguationData":[OSD([sQuery(id+"F0.wireOp",EDGE,"E42.0")])]})])],"derivedFrom":makeQuery(id+"F8.opExtrude","CAP_FACE",FACE,{"disambiguationData":[OSD([sQuery(id+"F0.wireOp",EDGE,"E26"),sQuery(id+"F0.wireOp",EDGE,"E28"),sQuery(id+"F2.wireOp",EDGE,"E57"),sQuery(id+"F2.wireOp",EDGE,"E58"),sQuery(id+"F2.wireOp",EDGE,"E60"),sQuery(id+"F2.wireOp",EDGE,"E62"),sQuery(id+"F2.wireOp",EDGE,"E63"),sQuery(id+"F2.wireOp",EDGE,"E64"),sQuery(id+"F2.wireOp",EDGE,"E65"),sQuery(id+"F2.wireOp",EDGE,"E68"),sQuery(id+"F2.wireOp",EDGE,"E69"),sQuery(id+"F2.wireOp",EDGE,"E70"),sQuery(id+"F2.wireOp",EDGE,"E71"),sQuery(id+"F2.wireOp",EDGE,"E72"),sQuery(id+"F2.wireOp",EDGE,"E73"),sQuery(id+"F2.wireOp",EDGE,"E74"),sQuery(id+"F2.wireOp",EDGE,"E75"),sQuery(id+"F2.wireOp",EDGE,"E87"),sQuery(id+"F2.wireOp",EDGE,"E94"),sQuery(id+"F2.wireOp",EDGE,"E96"),sQuery(id+"F2.wireOp",EDGE,"E98"),sQuery(id+"F2.wireOp",EDGE,"E99"),sQuery(id+"F2.wireOp",EDGE,"E100"),sQuery(id+"F2.wireOp",EDGE,"E104"),sQuery(id+"F2.wireOp",EDGE,"E105"),sQuery(id+"F2.wireOp",EDGE,"E106"),sQuery(id+"F4.wireOp",EDGE,"E107"),sQuery(id+"F4.wireOp",EDGE,"E108"),sQuery(id+"F4.wireOp",EDGE,"E109"),sQuery(id+"F6.wireOp",EDGE,"E110"),sQuery(id+"F6.wireOp",EDGE,"E111"),sQuery(id+"F6.wireOp",EDGE,"E112"),subQ6,sQuery(id+"F6.wireOp",EDGE,"E116"),sQuery(id+"F6.wireOp",EDGE,"E118"),sQuery(id+"F6.wireOp",EDGE,"E119"),sQuery(id+"F6.wireOp",EDGE,"E120"),sQuery(id+"F6.wireOp",EDGE,"E121"),sQuery(id+"F6.wireOp",EDGE,"E122"),sQuery(id+"F6.wireOp",EDGE,"E123"),sQuery(id+"F6.wireOp",EDGE,"E124"),sQuery(id+"F6.wireOp",EDGE,"E125"),sQuery(id+"F6.wireOp",EDGE,"E126"),sQuery(id+"F6.wireOp",EDGE,"E128"),sQuery(id+"F6.wireOp",EDGE,"E131.trimOffspring")])],"isStart":true})});}
            extrude(context, id + "F24", {"entities" : qUnion([Q0]), "operationType" : NewBodyOperationType.ADD, "depth" : 1 * mm});
        }
        {
            var Q0;
            {var subQ0=sQuery(id+"F6.wireOp",EDGE,"E128");var subQ1=sQuery(id+"F2.wireOp",EDGE,"E106");Q0=makeQuery(id+"F16.boolean.opBoolean","MERGE",EDGE,{"derivedFrom":[makeQuery(id+"F14.boolean.opBoolean","MERGE",EDGE,{"derivedFrom":[makeQuery(id+"F8.opExtrude","SWEPT_EDGE",EDGE,{"disambiguationData":[OSD([subQ1,subQ0,sQuery(id+"F6.wireOp",EDGE,"E130")])]}),makeQuery(id+"F14.opExtrude","SWEPT_EDGE",EDGE,{"disambiguationData":[OSD([subQ1,subQ0])]})]}),makeQuery(id+"F16.opExtrude","SWEPT_EDGE",EDGE,{"disambiguationData":[OSD([subQ1,subQ0,sQuery(id+"F13.wireOp",EDGE,"E142")])]})]});}
            var Q1;
            {var subQ0=sQuery(id+"F6.wireOp",EDGE,"E128");var subQ1=sQuery(id+"F2.wireOp",EDGE,"E105");var subQ2=sQuery(id+"F2.wireOp",EDGE,"E94");var subQ3=sQuery(id+"F2.wireOp",EDGE,"E68");var subQ4=sQuery(id+"F2.wireOp",EDGE,"E58");Q1=makeQuery(id+"F16.boolean.opBoolean","MERGE",EDGE,{"derivedFrom":[makeQuery(id+"F14.boolean.opBoolean","MERGE",EDGE,{"derivedFrom":[makeQuery(id+"F8.opExtrude","SWEPT_EDGE",EDGE,{"disambiguationData":[OSD([subQ4,subQ3,subQ2,subQ1,subQ0,sQuery(id+"F6.wireOp",EDGE,"E129")])]}),makeQuery(id+"F14.opExtrude","SWEPT_EDGE",EDGE,{"disambiguationData":[OSD([subQ4,subQ3,subQ2,subQ1,subQ0])]})]}),makeQuery(id+"F16.opExtrude","SWEPT_EDGE",EDGE,{"disambiguationData":[OSD([subQ4,subQ3,subQ2,subQ1,subQ0])]})]});}
            var Q2;
            {var subQ0=sQuery(id+"F6.wireOp",EDGE,"E131.trimOffspring");var subQ1=sQuery(id+"F2.wireOp",EDGE,"E98");var subQ2=sQuery(id+"F2.wireOp",EDGE,"E75");Q2=makeQuery(id+"F16.boolean.opBoolean","MERGE",EDGE,{"derivedFrom":[makeQuery(id+"F14.boolean.opBoolean","MERGE",EDGE,{"derivedFrom":[makeQuery(id+"F8.opExtrude","SWEPT_EDGE",EDGE,{"disambiguationData":[OSD([subQ2,subQ1,subQ0])]}),makeQuery(id+"F14.opExtrude","SWEPT_EDGE",EDGE,{"disambiguationData":[OSD([subQ2,subQ1,subQ0])]})]}),makeQuery(id+"F16.opExtrude","SWEPT_EDGE",EDGE,{"disambiguationData":[OSD([subQ2,subQ1,subQ0])]})]});}
            var Q3;
            {var subQ0=sQuery(id+"F6.wireOp",EDGE,"E131.trimOffspring");var subQ1=sQuery(id+"F2.wireOp",EDGE,"E96");var subQ2=sQuery(id+"F2.wireOp",EDGE,"E62");Q3=makeQuery(id+"F16.boolean.opBoolean","MERGE",EDGE,{"derivedFrom":[makeQuery(id+"F14.boolean.opBoolean","MERGE",EDGE,{"derivedFrom":[makeQuery(id+"F8.opExtrude","SWEPT_EDGE",EDGE,{"disambiguationData":[OSD([subQ2,subQ1,subQ0])]}),makeQuery(id+"F14.opExtrude","SWEPT_EDGE",EDGE,{"disambiguationData":[OSD([subQ2,subQ1,subQ0])]})]}),makeQuery(id+"F16.opExtrude","SWEPT_EDGE",EDGE,{"disambiguationData":[OSD([subQ2,subQ1,subQ0,sQuery(id+"F13.wireOp",EDGE,"E143")])]})]});}
            fillet(context, id + "F25", {"entities" : qUnion([Q0, Q1, Q2, Q3]), "radius" : .5 * mm, "tangentPropagation" : true, "allowEdgeOverflow" : false});
        }
        {
            var Q0;
            Q0=makeQuery(id+"F16.opExtrude","CAP_EDGE",EDGE,{"disambiguationData":[OSD([sQuery(id+"F2.wireOp",EDGE,"E71")])],"isStart":false});
            var Q1;
            Q1=makeQuery(id+"F16.opExtrude","CAP_EDGE",EDGE,{"disambiguationData":[OSD([sQuery(id+"F2.wireOp",EDGE,"E75"),sQuery(id+"F2.wireOp",EDGE,"E98")])],"isStart":false});
            var Q2;
            Q2=makeQuery(id+"F16.opExtrude","CAP_EDGE",EDGE,{"disambiguationData":[OSD([sQuery(id+"F2.wireOp",EDGE,"E58"),sQuery(id+"F2.wireOp",EDGE,"E68"),sQuery(id+"F2.wireOp",EDGE,"E94"),sQuery(id+"F2.wireOp",EDGE,"E105")])],"isStart":false});
            var Q3;
            {var subQ0=sQuery(id+"F13.wireOp",EDGE,"E141");Q3=makeQuery(id+"F16.opExtrude","CAP_EDGE",EDGE,{"disambiguationData":[OSD([subQ0]),TDD([makeQuery(id+"F15.imprint","IMPRINT",EDGE,{"derivedFrom":makeQuery(id+"F14.opExtrude","CAP_EDGE",EDGE,{"disambiguationData":[OSD([subQ0]),TDD([makeQuery(id+"F13.imprint","IMPRINT",EDGE,{"disambiguationData":[TD([[makeQuery(id+"F13.imprint","INTERSECT",VERTEX,{"derivedFrom":[makeQuery(id+"F8.opExtrude","CAP_EDGE",EDGE,{"disambiguationData":[OSD([sQuery(id+"F6.wireOp",EDGE,"E116"),sQuery(id+"F6.wireOp",EDGE,"E125")])],"isStart":false}),subQ0]}),-1.0]])],"derivedFrom":subQ0})])],"isStart":false})})])],"isStart":false});}
            fillet(context, id + "F26", {"entities" : qUnion([Q0, Q1, Q2, Q3]), "radius" : 3.5 * mm, "tangentPropagation" : true, "allowEdgeOverflow" : false});
        }
    });
